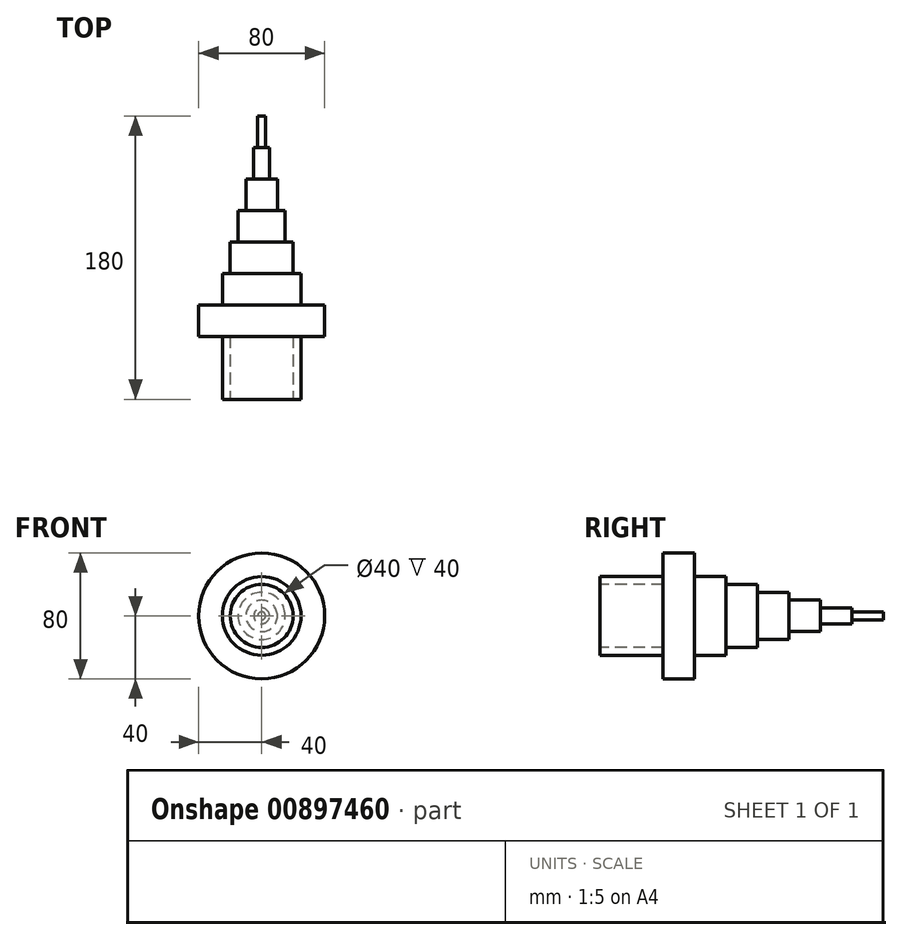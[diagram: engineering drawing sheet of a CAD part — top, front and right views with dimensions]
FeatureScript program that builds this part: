
annotation { "Feature Type Name" : "Feature", "Feature Type Description" : "" }
export const myFeature = defineFeature(function(context is Context, id is Id, definition is map)
    precondition{}
    {
        {
            var Q0;
            Q0=qCreatedBy(makeId("Front.planeOp"),FACE);
            var sketch = newSketch(context, id + "F0", { "sketchPlane" : qUnion([Q0])});
            skCircle(sketch, "E0", {"center": v(0, 0) * mm, "radius": 40 * mm});
            skSolve(sketch);
        }
        {
            var Q0;
            Q0 = qSketchRegion(id + "F0", true);
            extrude(context, id + "F1", {"entities" : qUnion([Q0]), "depth" : 20 * mm, "offsetDistance" : 25.4 * mm});
        }
        {
            var Q0;
            Q0=makeQuery(id+"F1.opExtrude","CAP_FACE",FACE,{"disambiguationData":[OSD([sQuery(id+"F0.wireOp",EDGE,"E0")])],"isStart":false});
            var sketch = newSketch(context, id + "F2", { "sketchPlane" : qUnion([Q0])});
            skCircle(sketch, "E1", {"center": v(0, 0) * mm, "radius": 25 * mm});
            skSolve(sketch);
        }
        {
            var Q0;
            Q0=makeQuery(id+"F2.imprint","IMPRINT",FACE,{"disambiguationData":[TD([[makeQuery(id+"F2.imprint","IMPRINT",EDGE,{"derivedFrom":sQuery(id+"F2.wireOp",EDGE,"E1")}),1.0]])]});
            var Q1;
            Q1=sQuery(id+"F2.wireOp",EDGE,"E1");
            extrude(context, id + "F3", {"entities" : qUnion([Q0]), "operationType" : NewBodyOperationType.ADD, "surfaceEntities" : qUnion([Q1]), "depth" : 40 * mm, "offsetDistance" : 25.4 * mm});
        }
        {
            var Q0;
            Q0=makeQuery(id+"F3.opExtrude","CAP_FACE",FACE,{"disambiguationData":[OSD([sQuery(id+"F2.wireOp",EDGE,"E1")])],"isStart":false});
            var sketch = newSketch(context, id + "F4", { "sketchPlane" : qUnion([Q0])});
            skCircle(sketch, "E2", {"center": v(0, 0) * mm, "radius": 20 * mm});
            skSolve(sketch);
        }
        {
            var Q0;
            Q0 = qSketchRegion(id + "F4", true);
            extrude(context, id + "F5", {"entities" : qUnion([Q0]), "operationType" : NewBodyOperationType.REMOVE, "oppositeDirection" : true, "depth" : 40 * mm, "offsetDistance" : 25.4 * mm});
        }
        {
            var Q0;
            Q0=makeQuery(id+"F1.opExtrude","CAP_FACE",FACE,{"disambiguationData":[OSD([sQuery(id+"F0.wireOp",EDGE,"E0")])],"isStart":true});
            var sketch = newSketch(context, id + "F6", { "sketchPlane" : qUnion([Q0])});
            skCircle(sketch, "E3", {"center": v(0, 0) * mm, "radius": 25 * mm});
            skSolve(sketch);
        }
        {
            var Q0;
            Q0=makeQuery(id+"F6.imprint","IMPRINT",FACE,{"disambiguationData":[TD([[makeQuery(id+"F6.imprint","IMPRINT",EDGE,{"derivedFrom":sQuery(id+"F6.wireOp",EDGE,"E3")}),1.0]])]});
            var Q1;
            Q1=sQuery(id+"F6.wireOp",EDGE,"E3");
            extrude(context, id + "F7", {"entities" : qUnion([Q0]), "operationType" : NewBodyOperationType.ADD, "surfaceEntities" : qUnion([Q1]), "depth" : 20 * mm, "offsetDistance" : 25.4 * mm});
        }
        {
            var Q0;
            Q0=makeQuery(id+"F7.opExtrude","CAP_FACE",FACE,{"disambiguationData":[OSD([sQuery(id+"F6.wireOp",EDGE,"E3")])],"isStart":false});
            var sketch = newSketch(context, id + "F8", { "sketchPlane" : qUnion([Q0])});
            skCircle(sketch, "E4", {"center": v(0, 0) * mm, "radius": 20 * mm});
            skSolve(sketch);
        }
        {
            var Q0;
            Q0=makeQuery(id+"F8.imprint","IMPRINT",FACE,{"disambiguationData":[TD([[makeQuery(id+"F8.imprint","IMPRINT",EDGE,{"derivedFrom":sQuery(id+"F8.wireOp",EDGE,"E4")}),1.0]])]});
            var Q1;
            Q1=sQuery(id+"F8.wireOp",EDGE,"E4");
            extrude(context, id + "F9", {"entities" : qUnion([Q0]), "operationType" : NewBodyOperationType.ADD, "surfaceEntities" : qUnion([Q1]), "depth" : 20 * mm, "offsetDistance" : 25.4 * mm});
        }
        {
            var Q0;
            Q0=makeQuery(id+"F9.opExtrude","CAP_FACE",FACE,{"disambiguationData":[OSD([sQuery(id+"F8.wireOp",EDGE,"E4")])],"isStart":false});
            var sketch = newSketch(context, id + "F10", { "sketchPlane" : qUnion([Q0])});
            skCircle(sketch, "E5", {"center": v(0, 0) * mm, "radius": 15 * mm});
            skSolve(sketch);
        }
        {
            var Q0;
            Q0 = qSketchRegion(id + "F10", true);
            extrude(context, id + "F11", {"entities" : qUnion([Q0]), "operationType" : NewBodyOperationType.ADD, "depth" : 20 * mm, "offsetDistance" : 25.4 * mm});
        }
        {
            var Q0;
            Q0=makeQuery(id+"F11.opExtrude","CAP_FACE",FACE,{"disambiguationData":[OSD([sQuery(id+"F10.wireOp",EDGE,"E5")])],"isStart":false});
            var sketch = newSketch(context, id + "F12", { "sketchPlane" : qUnion([Q0])});
            skCircle(sketch, "E6", {"center": v(0, 0) * mm, "radius": 10 * mm});
            skSolve(sketch);
        }
        {
            var Q0;
            Q0 = qSketchRegion(id + "F12", true);
            extrude(context, id + "F13", {"entities" : qUnion([Q0]), "operationType" : NewBodyOperationType.ADD, "depth" : 20 * mm, "offsetDistance" : 25.4 * mm});
        }
        {
            var Q0;
            Q0=makeQuery(id+"F13.opExtrude","CAP_FACE",FACE,{"disambiguationData":[OSD([sQuery(id+"F12.wireOp",EDGE,"E6")])],"isStart":false});
            var sketch = newSketch(context, id + "F14", { "sketchPlane" : qUnion([Q0])});
            skCircle(sketch, "E7", {"center": v(0, 0) * mm, "radius": 5 * mm});
            skSolve(sketch);
        }
        {
            var Q0;
            Q0 = qSketchRegion(id + "F14", true);
            extrude(context, id + "F15", {"entities" : qUnion([Q0]), "operationType" : NewBodyOperationType.ADD, "depth" : 20 * mm, "offsetDistance" : 25.4 * mm});
        }
        {
            var Q0;
            Q0=makeQuery(id+"F15.opExtrude","CAP_FACE",FACE,{"disambiguationData":[OSD([sQuery(id+"F14.wireOp",EDGE,"E7")])],"isStart":false});
            var sketch = newSketch(context, id + "F16", { "sketchPlane" : qUnion([Q0])});
            skCircle(sketch, "E8", {"center": v(0, 0) * mm, "radius": 2.5 * mm});
            skSolve(sketch);
        }
        {
            var Q0;
            Q0=makeQuery(id+"F16.imprint","IMPRINT",FACE,{"disambiguationData":[TD([[makeQuery(id+"F16.imprint","IMPRINT",EDGE,{"derivedFrom":sQuery(id+"F16.wireOp",EDGE,"E8")}),1.0]])]});
            var Q1;
            Q1=sQuery(id+"F16.wireOp",EDGE,"E8");
            extrude(context, id + "F17", {"entities" : qUnion([Q0]), "operationType" : NewBodyOperationType.ADD, "surfaceEntities" : qUnion([Q1]), "depth" : 20 * mm, "offsetDistance" : 25.4 * mm});
        }
    });
